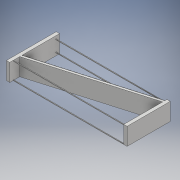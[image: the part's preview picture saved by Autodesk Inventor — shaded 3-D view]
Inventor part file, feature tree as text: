
AUTODESK INVENTOR PART (.ipt)
format: ipt  version: 2018.3 (Build 223284000, 284)  size: 421,376 bytes
history: native  units: mm
features: extrude x9, sketch x9
ambient origin geometry x8: Origin, YZ Plane, XZ Plane, XY Plane, X Axis, Y Axis, Z Axis, Center Point
bodies: Body1 (feature_tree)
feature tree (18):
  extrude  "Extrusion2"  Depth=30.0mm
  extrude  "Extrusion4"  Depth=3.0mm
  extrude  "Extrusion5"  Depth=3.0mm
  extrude  "Extrusion6"  Depth=15.7mm TaperAngle=0.0deg
  extrude  "Extrusion7"  Depth=0.5mm
  extrude  "Extrusion8"  Depth=100.0mm TaperAngle=0.0deg
  extrude  "Extrusion9"  Depth=9.0mm TaperAngle=0.0deg
  extrude  "Extrusion10"  Depth=10.66mm
  extrude  "Extrusion11"  Depth=4.0mm
  sketch  "Sketch2"  dims[d13=100.0mm d14=30.0mm]
  sketch  "Sketch4"  dims[d15=3.0mm d16=3.0mm]
  sketch  "Sketch5"  dims[d17=2.0mm d18=3.0mm]
  sketch  "Sketch6"  dims[d19=3.0mm d20=15.7mm d21=0.0mm]
  sketch  "Sketch7"  dims[d25=0.5mm d26=0.5mm]
  sketch  "Sketch8"  dims[d27=0.5mm d28=100.0mm d29=0.0mm]
  sketch  "Sketch9"  dims[d30=3.0mm d31=0.0mm d32=9.0mm d33=0.0mm]
  sketch  "Sketch11"  dims[d34=2.54mm d35=10.66mm]
  sketch  "Sketch12"  dims[d36=12.0mm d37=0.0mm d38=4.0mm d39=1.0mm d40=0.0mm d41=0.1mm d42=400.0mm d44=0.4mm d45=10.0mm d47=10.0mm d49=0.05mm d50=0.0mm d51=6.0mm d52=0.0mm d53=0.5mm d54=0.5mm d55=0.5mm d56=0.5mm d57=100.0mm d58=0.0mm d59=3.0mm]
